# Revit family: ledroad-st-p2_re488-20w-dali-730-xas_705000098800
name_source: partatom
category: Lighting Fixtures
units: mm (PartAtom-declared; Revit-internal decimal feet)

## family parameters
Cut with Voids When Loaded = No
Host = Face
Light Source = No
Part Type = Normal
Room Calculation Point = No
Round Connector Dimension = Use Diameter
Shared = No

## types (1)
- LEDRoad-St-P2 Re488-20W-DALI-730-XAS (1 x LED, 3000 lm, 3000)
    Apparent Load = 20 VA
    Approval mark = CE, ENEC
    CIE Flux Codes = 38 74 97 100 100
    Color Rendering = 70
    Color Temperature = 3000
    Control Gear = Electronic ballast
    Default Elevation = 1800 mm
    Description = Easy installation and maintenance via openable driver compartment . Flexible and adjustable pole connector (60mm & 76mm) for both side entry and pole top mounting (order separately).
    Frequency = 60 Hz
    Height = 100 mm  [stored 0.328084 ft]
    Lamp = 1 x LED
    Lamp Light Flux = 3000 lm
    Lamp count = 1
    Length = 488 mm
    Luminous efficacy = 150 lm/W
    Manufacturer = OPPLE
    ModVariant = No
    Model = 705000098800
    Mounting Place = Pole
    Mounting Type = Pole annexe
    Number of Poles = 1
    OnlyDefault = Yes
    Power Factor = 1
    Product Name = LEDRoad-St-P2 Re488-20W-DALI-730-XAS
    Product group = Street luminaire
    ProductGroupID = 15
    Protection Class = Protection class II
    Protection Degree = IP 66
    RLX_Detail_Level = 1
    RlxData = <blob elided: 200125 chars, md5=2cc0cdd8>
    Socket = socket
    Standby Power = 0 W
    System Light Flux = 3000 lm
    System Power = 20 W
    Type Comments = Product without accessories
    Type Image = stratus_v2.jpg
    URL = http://relux.com
    VarID = ---
    Voltage = 230 V
    Voltage Range = 220-240 V
    Weight = 0.00 kg
    Width = 255 mm

note: [stored X ft] marks values corroborated as IEEE doubles in the binary element streams (Revit-internal decimal feet)

## geometry (parser evidence)
native form markers: Blend x4, Sweep x10
no freeform markers — native parametric forms only
